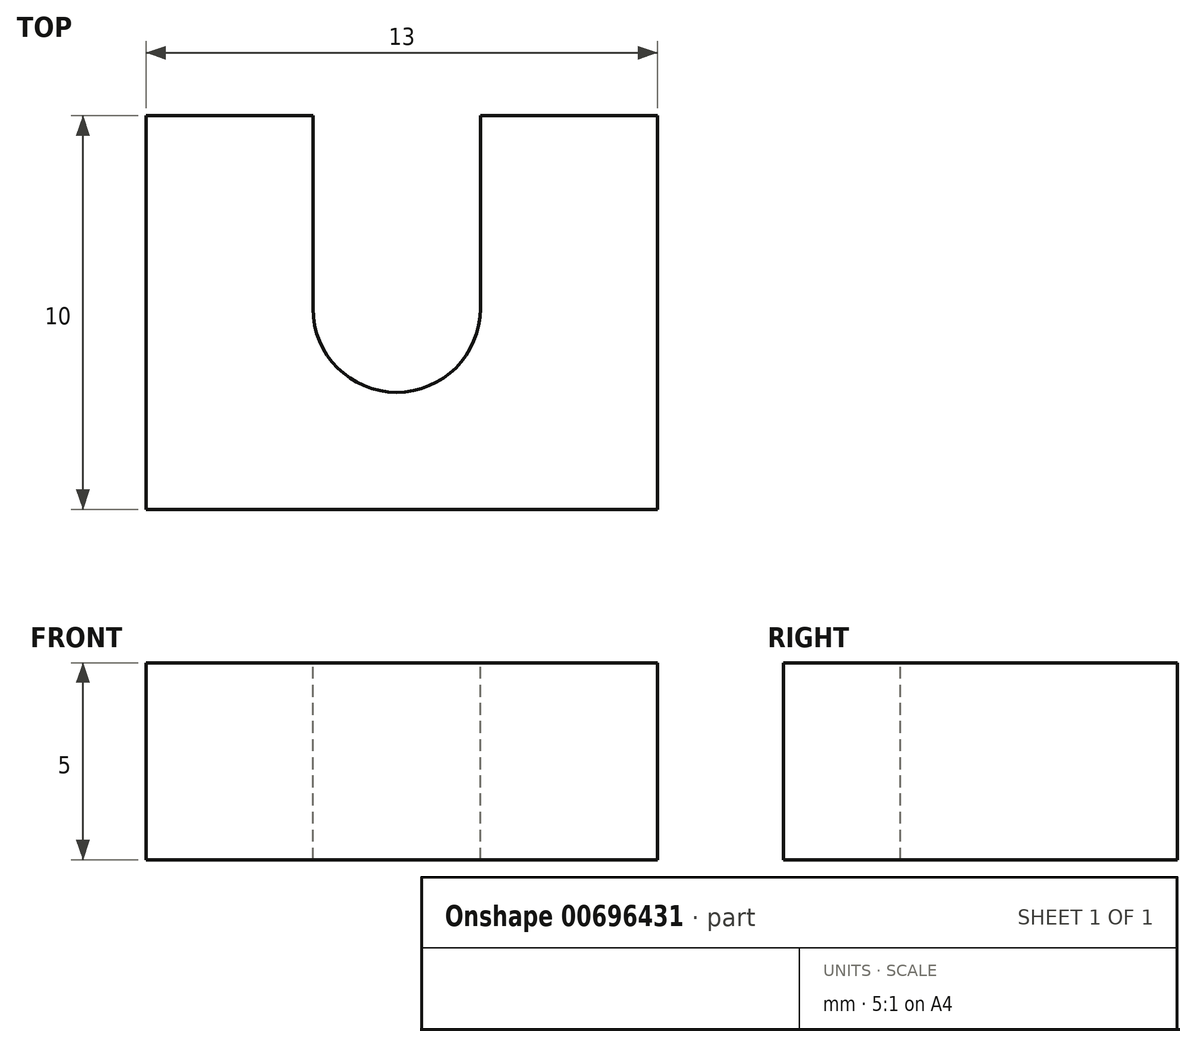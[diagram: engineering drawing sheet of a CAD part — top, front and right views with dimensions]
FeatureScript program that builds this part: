
annotation { "Feature Type Name" : "Feature", "Feature Type Description" : "" }
export const myFeature = defineFeature(function(context is Context, id is Id, definition is map)
    precondition{}
    {
        {
            var Q0;
            Q0=qCreatedBy(makeId("Top.planeOp"),FACE);
            var sketch = newSketch(context, id + "F0", { "sketchPlane" : qUnion([Q0])});
            skLineSegment(sketch, "E0.bottom", {"start": v(-6.37, 4.9) * mm, "end": v(6.63, 4.9) * mm});
            skLineSegment(sketch, "E0.top", {"start": v(-6.37, -5.1) * mm, "end": v(6.63, -5.1) * mm});
            skLineSegment(sketch, "E0.left", {"start": v(-6.37, 4.9) * mm, "end": v(-6.37, -5.1) * mm});
            skLineSegment(sketch, "E0.right", {"start": v(6.63, 4.9) * mm, "end": v(6.63, -5.1) * mm});
            skSolve(sketch);
        }
        {
            var Q0;
            Q0 = qSketchRegion(id + "F0", true);
            extrude(context, id + "F1", {"entities" : qUnion([Q0]), "depth" : 5 * mm, "offsetDistance" : 25 * mm});
        }
        {
            var Q0;
            Q0=makeQuery(id+"F1.opExtrude","CAP_FACE",FACE,{"disambiguationData":[OSD([sQuery(id+"F0.wireOp",EDGE,"E0.bottom"),sQuery(id+"F0.wireOp",EDGE,"E0.top"),sQuery(id+"F0.wireOp",EDGE,"E0.left"),sQuery(id+"F0.wireOp",EDGE,"E0.right")])],"isStart":false});
            var sketch = newSketch(context, id + "F2", { "sketchPlane" : qUnion([Q0])});
            skArc(sketch, "E1", {"start": v(-2.12, 0) * mm, "mid": v(0, -2.12) * mm, "end": v(2.12, 0) * mm});
            skLineSegment(sketch, "E2", {"start": v(-2.12, 0) * mm, "end": v(-2.12, 4.9) * mm});
            skLineSegment(sketch, "E3", {"start": v(2.12, 0) * mm, "end": v(2.12, 4.9) * mm});
            skSolve(sketch);
        }
        {
            var Q0;
            Q0 = qSketchRegion(id + "F2", true);
            var Q1;
            Q1=makeQuery(id+"F2.imprint","IMPRINT",FACE,{"disambiguationData":[TD([[makeQuery(id+"F2.imprint","IMPRINT",EDGE,{"derivedFrom":sQuery(id+"F2.wireOp",EDGE,"E1")}),1.0]])]});
            extrude(context, id + "F3", {"entities" : qUnion([Q0, Q1]), "operationType" : NewBodyOperationType.REMOVE, "oppositeDirection" : true, "depth" : 10 * mm, "offsetDistance" : 25 * mm});
        }
    });
